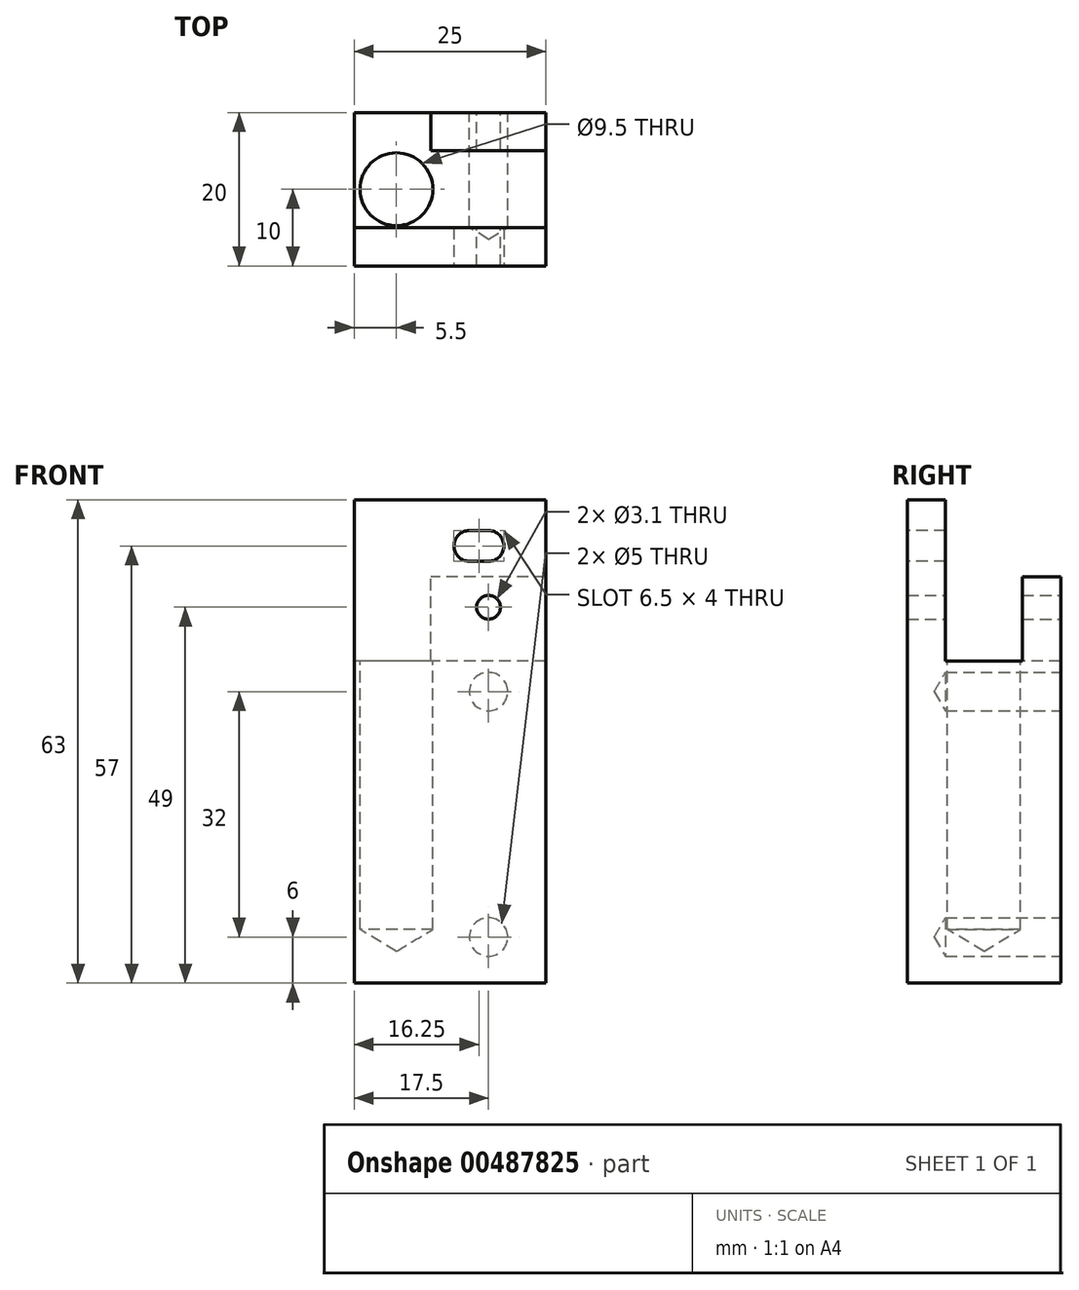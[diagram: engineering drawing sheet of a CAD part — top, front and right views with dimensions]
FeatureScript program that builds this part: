
annotation { "Feature Type Name" : "Feature", "Feature Type Description" : "" }
export const myFeature = defineFeature(function(context is Context, id is Id, definition is map)
    precondition{}
    {
        {
            var Q0;
            Q0=qCreatedBy(makeId("Front.planeOp"),FACE);
            var sketch = newSketch(context, id + "F0", { "sketchPlane" : qUnion([Q0])});
            skLineSegment(sketch, "E0.bottom", {"start": v(0, 0) * mm, "end": v(25, 0) * mm});
            skLineSegment(sketch, "E0.top", {"start": v(0, -60) * mm, "end": v(25, -60) * mm});
            skLineSegment(sketch, "E0.left", {"start": v(0, 0) * mm, "end": v(0, -60) * mm});
            skLineSegment(sketch, "E0.right", {"start": v(25, 0) * mm, "end": v(25, -60) * mm});
            skSolve(sketch);
        }
        {
            var Q0;
            Q0 = qSketchRegion(id + "F0", true);
            extrude(context, id + "F1", {"entities" : qUnion([Q0]), "depth" : 20 * mm, "offsetDistance" : 25 * mm});
        }
        {
            var Q0;
            Q0=makeQuery(id+"F1.opExtrude","SWEPT_FACE",FACE,{"disambiguationData":[OSD([sQuery(id+"F0.wireOp",EDGE,"E0.left")])]});
            var sketch = newSketch(context, id + "F2", { "sketchPlane" : qUnion([Q0])});
            skLineSegment(sketch, "E1.bottom", {"start": v(15, -18) * mm, "end": v(5, -18) * mm});
            skLineSegment(sketch, "E1.top", {"start": v(15, 18) * mm, "end": v(5, 18) * mm});
            skLineSegment(sketch, "E1.left", {"start": v(15, -18) * mm, "end": v(15, 18) * mm});
            skLineSegment(sketch, "E1.right", {"start": v(5, -18) * mm, "end": v(5, 18) * mm});
            skPoint(sketch, "E1.middle", {"position": v(10, 0) * mm});
            skSolve(sketch);
        }
        {
            var Q0;
            {var subQ0=sQuery(id+"F2.wireOp",EDGE,"E1.bottom");Q0=makeQuery(id+"F2.imprint","IMPRINT",FACE,{"disambiguationData":[TD([[makeQuery(id+"F2.imprint","IMPRINT",EDGE,{"derivedFrom":subQ0}),-1.0]])]});}
            extrude(context, id + "F3", {"entities" : qUnion([Q0]), "operationType" : NewBodyOperationType.REMOVE, "endBound" : BoundingType.THROUGH_ALL, "oppositeDirection" : true, "depth" : 25 * mm, "offsetDistance" : 25 * mm});
        }
        {
            var Q0;
            Q0=makeQuery(id+"F1.opExtrude","SWEPT_FACE",FACE,{"disambiguationData":[OSD([sQuery(id+"F0.wireOp",EDGE,"E0.left")])]});
            var sketch = newSketch(context, id + "F4", { "sketchPlane" : qUnion([Q0])});
            skLineSegment(sketch, "E2.bottom", {"start": v(0, 0) * mm, "end": v(5, 0) * mm});
            skLineSegment(sketch, "E2.top", {"start": v(0, -7) * mm, "end": v(5, -7) * mm});
            skLineSegment(sketch, "E2.left", {"start": v(0, 0) * mm, "end": v(0, -7) * mm});
            skLineSegment(sketch, "E2.right", {"start": v(5, 0) * mm, "end": v(5, -7) * mm});
            skSolve(sketch);
        }
        {
            var Q0;
            Q0=makeQuery(id+"F4.imprint","IMPRINT",FACE,{"disambiguationData":[TD([[makeQuery(id+"F4.imprint","IMPRINT",EDGE,{"derivedFrom":sQuery(id+"F4.wireOp",EDGE,"E2.bottom")}),1.0]])]});
            extrude(context, id + "F5", {"entities" : qUnion([Q0]), "operationType" : NewBodyOperationType.REMOVE, "endBound" : BoundingType.THROUGH_ALL, "oppositeDirection" : true, "depth" : 25 * mm, "offsetDistance" : 25 * mm});
        }
        {
            var Q0;
            Q0=makeQuery(id+"F1.opExtrude","CAP_FACE",FACE,{"disambiguationData":[OSD([sQuery(id+"F0.wireOp",EDGE,"E0.bottom"),sQuery(id+"F0.wireOp",EDGE,"E0.top"),sQuery(id+"F0.wireOp",EDGE,"E0.left"),sQuery(id+"F0.wireOp",EDGE,"E0.right")])],"isStart":true});
            var sketch = newSketch(context, id + "F6", { "sketchPlane" : qUnion([Q0])});
            skPoint(sketch, "E3", {"position": v(-17.5, -11) * mm});
            skSolve(sketch);
        }
        {
            var Q0;
            Q0=sQuery(id+"F6.wireOp",VERTEX,"E3");
            var Q1;
            Q1=makeQuery(id+"F1.opExtrude","SWEPT_BODY",BODY,{"disambiguationData":[OSD([sQuery(id+"F0.wireOp",EDGE,"E0.bottom"),sQuery(id+"F0.wireOp",EDGE,"E0.top"),sQuery(id+"F0.wireOp",EDGE,"E0.left"),sQuery(id+"F0.wireOp",EDGE,"E0.right")])]});
            hole(context, id + "F7", {"style" : HoleStyle.SIMPLE, "endStyle" : HoleEndStyle.THROUGH, "holeDiameter" : 3.1 * mm, "isTappedThrough" : true, "tappedDepth" : 12 * mm, "tapClearance" : 3, "locations" : qUnion([Q0]), "scope" : qUnion([Q1])});
        }
        {
            var Q0;
            Q0=makeQuery(id+"F3.boolean.opBoolean","COPY",FACE,{"derivedFrom":makeQuery(id+"F3.opExtrude","SWEPT_FACE",FACE,{"disambiguationData":[OSD([sQuery(id+"F2.wireOp",EDGE,"E1.bottom")])]})});
            var sketch = newSketch(context, id + "F8", { "sketchPlane" : qUnion([Q0])});
            skPoint(sketch, "E4", {"position": v(5.5, -10) * mm});
            skSolve(sketch);
        }
        {
            var Q0;
            Q0=sQuery(id+"F8.wireOp",VERTEX,"E4");
            var Q1;
            Q1=makeQuery(id+"F1.opExtrude","SWEPT_BODY",BODY,{"disambiguationData":[OSD([sQuery(id+"F0.wireOp",EDGE,"E0.bottom"),sQuery(id+"F0.wireOp",EDGE,"E0.top"),sQuery(id+"F0.wireOp",EDGE,"E0.left"),sQuery(id+"F0.wireOp",EDGE,"E0.right")])]});
            hole(context, id + "F9", {"style" : HoleStyle.SIMPLE, "endStyle" : HoleEndStyle.BLIND, "holeDiameter" : 9.5 * mm, "holeDepth" : 35 * mm, "isTappedThrough" : true, "tappedDepth" : 12 * mm, "tapClearance" : 3, "locations" : qUnion([Q0]), "scope" : qUnion([Q1])});
        }
        {
            var Q0;
            Q0=makeQuery(id+"F1.opExtrude","CAP_FACE",FACE,{"disambiguationData":[OSD([sQuery(id+"F0.wireOp",EDGE,"E0.bottom"),sQuery(id+"F0.wireOp",EDGE,"E0.top"),sQuery(id+"F0.wireOp",EDGE,"E0.left"),sQuery(id+"F0.wireOp",EDGE,"E0.right")])],"isStart":false});
            var sketch = newSketch(context, id + "F10", { "sketchPlane" : qUnion([Q0])});
            skArc(sketch, "E5", {"start": v(15, -1) * mm, "mid": v(13, -3) * mm, "end": v(15, -5) * mm});
            skArc(sketch, "E6", {"start": v(17.5, -5) * mm, "mid": v(19.5, -3) * mm, "end": v(17.5, -1) * mm});
            skLineSegment(sketch, "E7.bottom", {"start": v(17.5, -1) * mm, "end": v(15, -1) * mm});
            skLineSegment(sketch, "E7.top", {"start": v(17.5, -5) * mm, "end": v(15, -5) * mm});
            skPoint(sketch, "E7.right.end.orphan", {"position": v(12.5, -5) * mm});
            skPoint(sketch, "E7.right.start.orphan", {"position": v(12.5, -1) * mm});
            skSolve(sketch);
        }
        {
            var Q0;
            Q0=makeQuery(id+"F10.imprint","IMPRINT",FACE,{"disambiguationData":[TD([[makeQuery(id+"F10.imprint","IMPRINT",EDGE,{"derivedFrom":sQuery(id+"F10.wireOp",EDGE,"E5")}),1.0]])]});
            extrude(context, id + "F11", {"entities" : qUnion([Q0]), "operationType" : NewBodyOperationType.REMOVE, "endBound" : BoundingType.THROUGH_ALL, "oppositeDirection" : true, "depth" : 25 * mm, "offsetDistance" : 25 * mm});
        }
        {
            var Q0;
            Q0=makeQuery(id+"F1.opExtrude","CAP_FACE",FACE,{"disambiguationData":[OSD([sQuery(id+"F0.wireOp",EDGE,"E0.bottom"),sQuery(id+"F0.wireOp",EDGE,"E0.top"),sQuery(id+"F0.wireOp",EDGE,"E0.left"),sQuery(id+"F0.wireOp",EDGE,"E0.right")])],"isStart":true});
            var sketch = newSketch(context, id + "F12", { "sketchPlane" : qUnion([Q0])});
            skPoint(sketch, "E8", {"position": v(-17.5, -22) * mm});
            skPoint(sketch, "E9", {"position": v(-17.5, -54) * mm});
            skSolve(sketch);
        }
        {
            var Q0;
            Q0=sQuery(id+"F12.wireOp",VERTEX,"E9");
            var Q1;
            Q1=sQuery(id+"F12.wireOp",VERTEX,"E8");
            var Q2;
            Q2=makeQuery(id+"F1.opExtrude","SWEPT_BODY",BODY,{"disambiguationData":[OSD([sQuery(id+"F0.wireOp",EDGE,"E0.bottom"),sQuery(id+"F0.wireOp",EDGE,"E0.top"),sQuery(id+"F0.wireOp",EDGE,"E0.left"),sQuery(id+"F0.wireOp",EDGE,"E0.right")])]});
            hole(context, id + "F13", {"style" : HoleStyle.SIMPLE, "endStyle" : HoleEndStyle.BLIND, "standardTappedOrClearance" : lookupTablePath({ "standard" : "ISO", "engagement" : "75%", "pitch" : "1 mm", "size" : "M6", "type" : "Tapped" }), "standardBlindInLast" : lookupTablePath({ "standard" : "ISO", "engagement" : "75%", "pitch" : "1 mm", "size" : "M6", "type" : "Tapped" }), "holeDiameter" : 5 * mm, "showTappedDepth" : true, "holeDepth" : 15 * mm, "isTappedThrough" : true, "tappedDepth" : 12 * mm, "tapClearance" : 3, "locations" : qUnion([Q0, Q1]), "scope" : qUnion([Q2]), "majorDiameter" : 6 * mm});
        }
        {
            var Q0;
            {var subQ2=sQuery(id+"F0.wireOp",EDGE,"E0.bottom");Q0=makeQuery(id+"F3.boolean.opBoolean","SPLIT",FACE,{"disambiguationData":[TD([makeQuery(id+"F3.opExtrude","SWEPT_FACE",FACE,{"disambiguationData":[OSD([sQuery(id+"F2.wireOp",EDGE,"E1.left")])]})])],"derivedFrom":makeQuery(id+"F1.opExtrude","SWEPT_FACE",FACE,{"disambiguationData":[OSD([subQ2])]})});}
            extrude(context, id + "F14", {"entities" : qUnion([Q0]), "operationType" : NewBodyOperationType.ADD, "depth" : 3 * mm, "offsetDistance" : 25 * mm});
        }
        {
            var Q0;
            Q0=makeQuery(id+"F3.boolean.opBoolean","COPY",FACE,{"derivedFrom":makeQuery(id+"F3.opExtrude","SWEPT_FACE",FACE,{"disambiguationData":[OSD([sQuery(id+"F2.wireOp",EDGE,"E1.right")])]})});
            var sketch = newSketch(context, id + "F15", { "sketchPlane" : qUnion([Q0])});
            skLineSegment(sketch, "E10.bottom", {"start": v(0, -18) * mm, "end": v(10, -18) * mm});
            skLineSegment(sketch, "E10.top", {"start": v(0, -7) * mm, "end": v(10, -7) * mm});
            skLineSegment(sketch, "E10.left", {"start": v(0, -18) * mm, "end": v(0, -7) * mm});
            skLineSegment(sketch, "E10.right", {"start": v(10, -18) * mm, "end": v(10, -7) * mm});
            skSolve(sketch);
        }
        {
            var Q0;
            Q0=makeQuery(id+"F15.imprint","IMPRINT",FACE,{"disambiguationData":[TD([[makeQuery(id+"F15.imprint","IMPRINT",EDGE,{"derivedFrom":sQuery(id+"F15.wireOp",EDGE,"E10.bottom")}),-1.0]])]});
            extrude(context, id + "F16", {"entities" : qUnion([Q0]), "operationType" : NewBodyOperationType.REMOVE, "endBound" : BoundingType.THROUGH_ALL, "oppositeDirection" : true, "depth" : 25 * mm, "offsetDistance" : 25 * mm});
        }
    });
